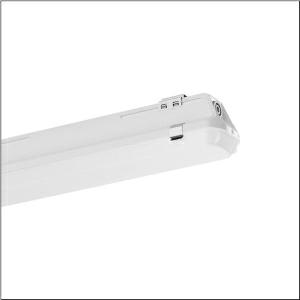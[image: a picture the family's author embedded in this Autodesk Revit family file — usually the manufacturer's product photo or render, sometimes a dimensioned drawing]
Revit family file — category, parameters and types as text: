
# Revit family: monsun_r__21_51fb107p460b_c23d
name_source: partatom
category: Lighting Fixtures
units: mm (PartAtom-declared; Revit-internal decimal feet)

## family parameters
Cut with Voids When Loaded = No
Host = Face
Light Source = No
Part Type = Normal
Room Calculation Point = No
Round Connector Dimension = Use Diameter
Shared = No

## types (1)
- Monsun® 21 (1 x LED, 6000 lm, 38 W, 4000K)
    Apparent Load = 38 VA
    CIE Flux Codes = 47 77 93 94 100
    Color Rendering = 80
    Color Temperature = 4000K
    Default Elevation = 1800 mm
    Description = Monsun® 21, damp-proof luminaire, chain hanger, primary optical cover: enclosure, of PMMA, light emission: direct distribution, primary light characteristic: symmetric, installation type: suspended mounting, surface-mounted, horizontal mounting, vertical mounting, LED, rated luminous flux: 6.000lm, luminous efficacy: 158lm/W, light colour: 840, colour temperature: 4000K, control gear: ECG, with terminal, 3-pole, max. 2.5mm², mains connection: 220..240V, AC, 50/60Hz, rated input power: 38W, housing, of glass-fibre reinforced polyester, uncoated, bright grey, incl. chain hanger, length: 1.590mm, width: 90mm, height: 88mm, clip for enclosure, of stainless steel (V2A), ceiling mounting element, of stainless steel (V2A), chain hanger, of stainless steel (V2A), protection rating (complete): IP66, insulation class (complete): insulation class I (protective earthing), certification: CE, ENEC, VDE, UKCA, protection symbol: D, impact resistance: IK04, permissible operating ambient temperature: -25..+35°C, standard: EN 50419, EN 60598-2-1, corresponds to IFS (International Featured Standards) requirements for safety and quality in the food industry, for indoor or canopied outdoor use, no direct snow, no direct sun, no direct rain, contact your sales advisor before using the luminaires in applications with unclear chemical exposure, large temperature fluctuations or condensation-forming humidity, LABS conformity tested according to VDMA 24364:2018-05, packaging unit: 1 piece
    Height = 89 mm
    Lamp = 1 x LED
    Lamp Light Flux = 6000 lm
    Lamp Power = 38 W
    Lamp count = 1
    Length = 1590 mm
    Luminous efficacy = 158 lm/W
    Manufacturer = Siteco
    ModVariant = No
    Model = 51FB107P460B
    Mounting Place = Ceiling
    Mounting Type = Surface mounted
    Number of Poles = 1
    OnlyDefault = Yes
    Power Factor = 1
    Product Name = Monsun® 21
    Product group = damp-proof luminaire
    ProductGroupID = 300
    Protection Class = Protection class I
    Protection Degree = IP 66
    RLX_Detail_Level = 1
    RLX_Emergency_Light_Flux = 0 lm
    RLX_Emergency_Type = 0
    RLX_Emergency_Type_DB = No
    RlxData = <blob elided: 88421 chars, md5=d228be7c>
    Socket = socket
    Standby Power = 0 W
    System Light Flux = 6000 lm
    System Power = 38 W
    Type Comments = Product without accessories
    Type Image = l_1006717.jpg
    URL = http://relux.com
    VarID = ---
    Voltage = 0 V
    Weight = 0.00 kg
    Width = 90 mm

## geometry (parser evidence)
native form markers: Blend x4, Sweep x14
no freeform markers — native parametric forms only
